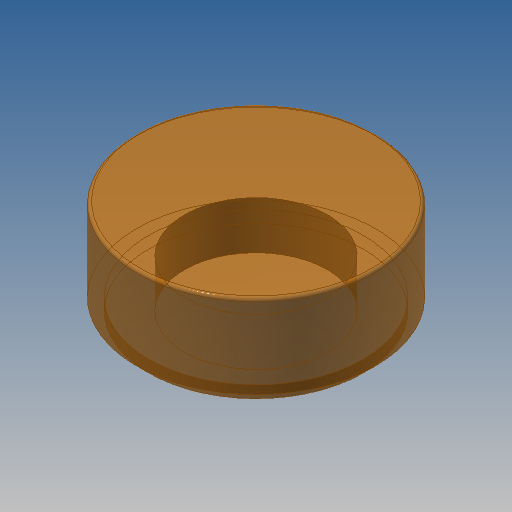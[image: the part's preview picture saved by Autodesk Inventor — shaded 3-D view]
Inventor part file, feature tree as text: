
AUTODESK INVENTOR PART (.ipt)
format: ipt  version: 2022.2 (Build 262287000, 287)  size: 148,480 bytes
history: native  units: in
note: dims shown in document units (in); Inventor stores cm internally (conversion verified against a paired STEP export)
features: extrude x3, sketch x2, fillet x1
ambient origin geometry x8: Origin, YZ Plane, XZ Plane, XY Plane, X Axis, Y Axis, Z Axis, Center Point
bodies: Solid1 (feature_tree)
feature tree (6):
  extrude  "Extrusion1"  Depth=0.315in
  sketch  "Sketch10"  dims[d4=0.126in d5=0.0in d7=0.0591in d22=0.0039in d92=0.189in d93=0.1575in d94=0.1575in d95=0.189in d96=0.063in d97=0.0in d98=0.0in d99=0.0157in d100=0.0157in d101=0.0in]
  extrude  "Extrusion6"  Depth=0.0039in
  extrude  "Extrusion7"  Depth=0.0157in
  fillet  "Fillet1"  Radius=0.1575in
  sketch  "Sketch2"  dims[d0=0.315in d1=0.315in]
